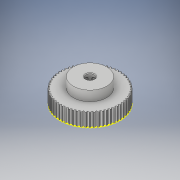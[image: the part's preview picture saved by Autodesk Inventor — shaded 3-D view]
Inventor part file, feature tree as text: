
AUTODESK INVENTOR PART (.ipt)
format: ipt  version: 2019.2 (Build 232265000, 265)  size: 1,153,024 bytes
history: native  units: mm
features: move_body x2, other x1, sketch x1, imported_body x1
ambient origin geometry x8: Origin, YZ Plane, XZ Plane, XY Plane, X Axis, Y Axis, Z Axis, Center Point
bodies: Solid1 (feature_tree)
feature tree (5):
  other  "gates_P60-3M-09AL.stp"
  move_body  "Move Body1"
  move_body  "Move Body2"
  sketch  "Sketch2"  dims[d0=90.0deg d1=90.0deg]
  imported_body  "Base1"
